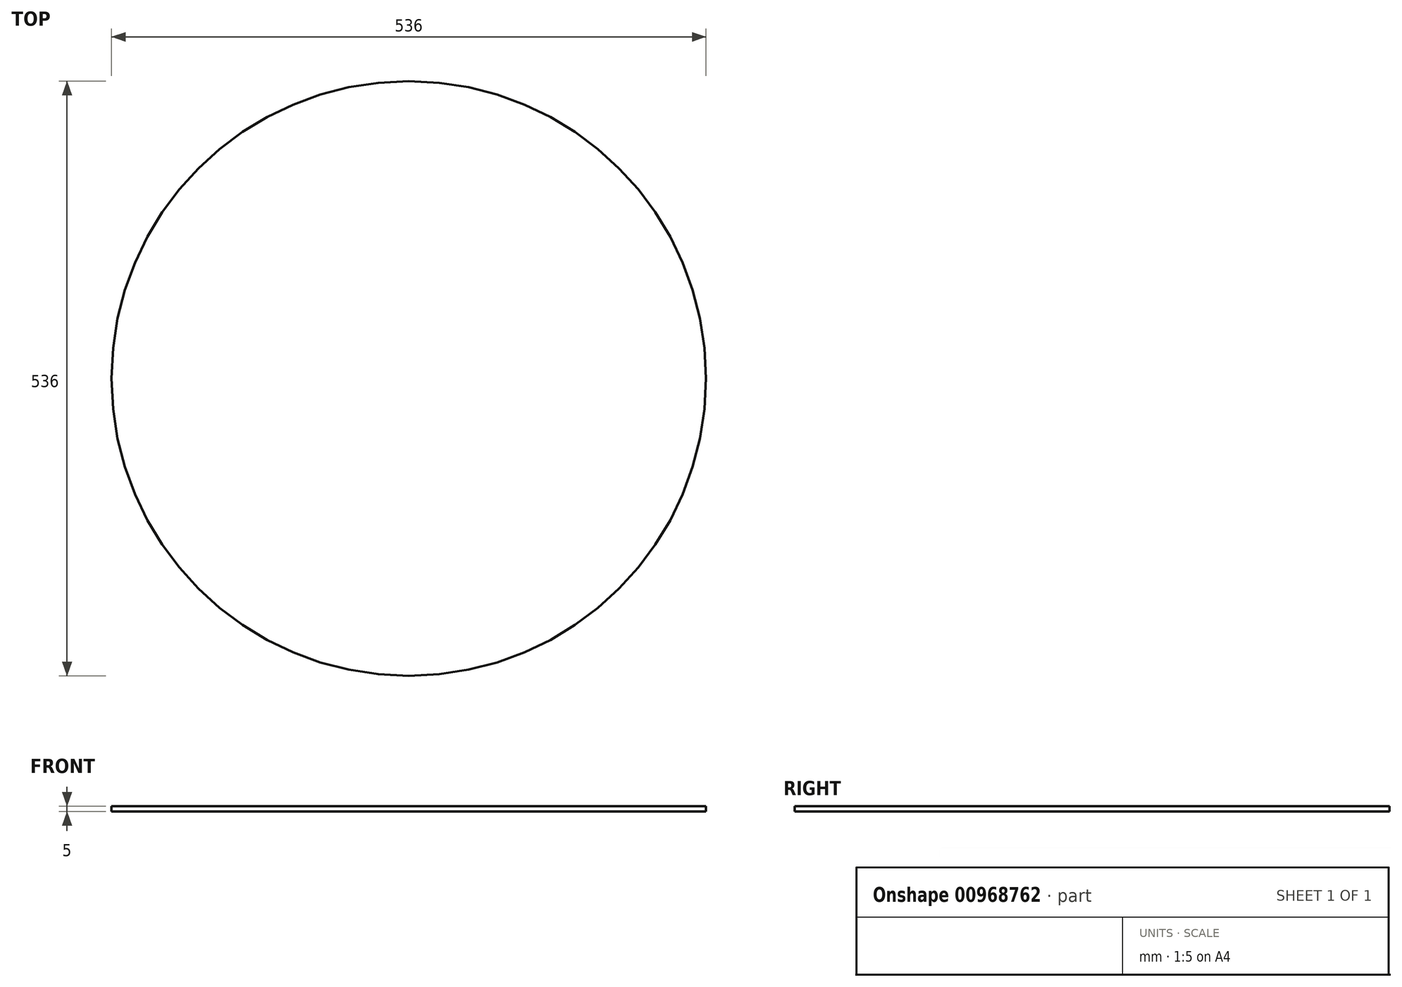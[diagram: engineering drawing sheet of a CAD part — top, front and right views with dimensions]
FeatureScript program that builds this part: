
annotation { "Feature Type Name" : "Feature", "Feature Type Description" : "" }
export const myFeature = defineFeature(function(context is Context, id is Id, definition is map)
    precondition{}
    {
        {
            var Q0;
            Q0=qCreatedBy(makeId("Top.planeOp"),FACE);
            var sketch = newSketch(context, id + "F0", { "sketchPlane" : qUnion([Q0])});
            skCircle(sketch, "E0", {"center": v(0, 0) * mm, "radius": 268 * mm});
            skSolve(sketch);
        }
        {
            var Q0;
            Q0 = qSketchRegion(id + "F0", true);
            extrude(context, id + "F1", {"entities" : qUnion([Q0]), "depth" : 5 * mm, "offsetDistance" : 25 * mm});
        }
    });
